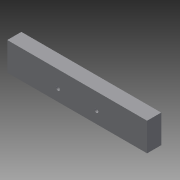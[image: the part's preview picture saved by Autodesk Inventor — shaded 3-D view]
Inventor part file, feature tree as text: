
AUTODESK INVENTOR PART (.ipt)
format: ipt  version: 2013 (Build 170138000, 138)  size: 168,960 bytes
history: native  units: mm
features: sketch x5, extrude x4, other x2, hole x1, fillet x1
ambient origin geometry x8: Origin, YZ Plane, XZ Plane, XY Plane, X Axis, Y Axis, Z Axis, Center Point
feature tree (13):
  other  "ソリッド1"
  extrude  "押し出し1"  Depth=109.0mm
  extrude  "押し出し3"  Depth=54.5mm
  extrude  "押し出し4"  Depth=20.0mm
  extrude  "押し出し5"  Depth=10.0mm
  hole  "穴1"  [1 undecoded]
  other  "リップ3"
  fillet  "フィレット1"  Radius=11.0mm
  sketch  "スケッチ1"
  sketch  "スケッチ4"
  sketch  "スケッチ5"
  sketch  "スケッチ6"
  sketch  "スケッチ7"
note: 1 required parameter value undecoded (feature->parameter linkage not recoverable at this tier; creation-order binding heuristic only, values carry confidence <= 0.55)
